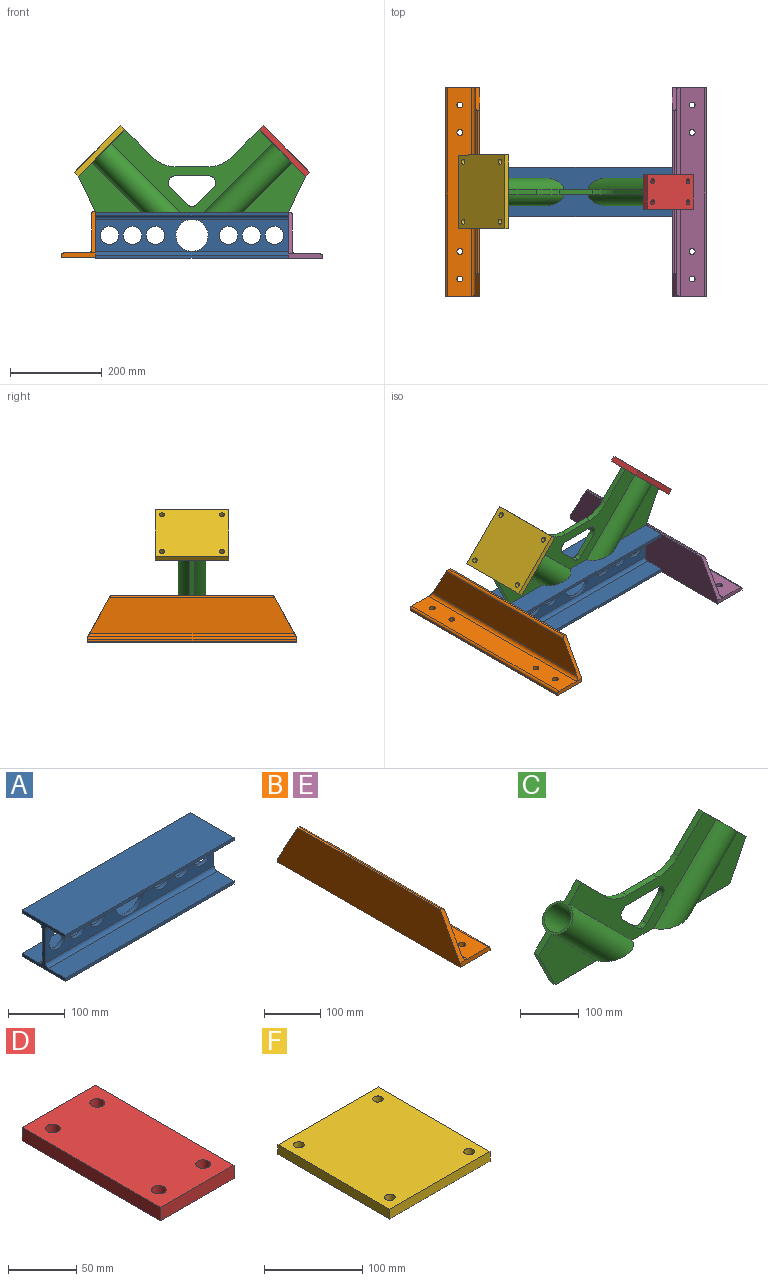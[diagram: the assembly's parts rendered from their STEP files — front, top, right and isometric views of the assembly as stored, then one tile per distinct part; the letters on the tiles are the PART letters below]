
ASSEMBLY  parts=6 mates=5
PART A: 25 faces, bbox 420x108x100 mm
  f0: plane 108x100mm, normal (1,0,0), area 2194.9mm2, adj f9,f10,f11,f12,f13,f14,f15,f16
  f1: cylinder r=35mm len=70mm, axis (0,1,0), area 1759.3mm2, adj f9,f10
  f2: cylinder r=20mm len=40mm, axis (0,1,0), area 1005.3mm2, adj f9,f10
  f3: cylinder r=20mm len=40mm, axis (0,1,0), area 1005.3mm2, adj f9,f10
  f4: cylinder r=20mm len=40mm, axis (0,1,0), area 1005.3mm2, adj f9,f10
  f5: cylinder r=20mm len=40mm, axis (0,1,0), area 1005.3mm2, adj f9,f10
  f6: cylinder r=20mm len=40mm, axis (0,1,0), area 1005.3mm2, adj f9,f10
  f7: cylinder r=20mm len=40mm, axis (0,1,0), area 1005.3mm2, adj f9,f10
  f8: plane 108x100mm, normal (-1,0,0), area 2194.9mm2, adj f9,f10,f11,f12,f13,f14,f15,f16
  f9: plane 420x70.6mm, normal (0,-1,0), area 18263.7mm2, adj f0,f1,f2,f3,f4,f5,f6,f7
  f10: plane 420x70.6mm, normal (0,1,0), area 18263.7mm2, adj f0,f1,f2,f3,f4,f5,f6,f7
  f11: plane 420x42mm, normal (0,0,1), area 17640mm2, adj f0,f8,f14,f24
  f12: plane 420x108mm, normal (0,0,-1), area 45360mm2, adj f0,f8,f14,f15
  f13: plane 420x42mm, normal (0,0,1), area 17640mm2, adj f0,f8,f15,f22
  f14: plane 420x6.7mm, normal (0,-1,0), area 2814mm2, adj f0,f8,f11,f12
  f15: plane 420x6.7mm, normal (0,1,0), area 2814mm2, adj f0,f8,f12,f13
  f16: plane 420x42mm, normal (0,0,-1), area 17640mm2, adj f0,f8,f19,f23
  f17: plane 420x42mm, normal (0,0,-1), area 17640mm2, adj f0,f8,f20,f21
  f18: plane 420x108mm, normal (0,0,1), area 45360mm2, adj f0,f8,f19,f20
  f19: plane 420x6.7mm, normal (0,-1,0), area 2814mm2, adj f0,f8,f16,f18
  f20: plane 420x6.7mm, normal (0,1,0), area 2814mm2, adj f0,f8,f17,f18
  f21: cylinder r=8mm len=420mm, axis (-1,0,0), area 5277.9mm2, adj f0,f8,f10,f17
  f22: cylinder r=8mm len=420mm, axis (1,0,0), area 5277.9mm2, adj f0,f8,f10,f13
  f23: cylinder r=8mm len=420mm, axis (1,0,0), area 5277.9mm2, adj f0,f8,f9,f16
  f24: cylinder r=8mm len=420mm, axis (-1,0,0), area 5277.9mm2, adj f0,f8,f9,f11
PART B: 17 faces, bbox 75x456x100 mm
  f0: plane 356x4.5mm, normal (0,0,1), area 1602mm2, adj f1,f9,f10,f12
  f1: plane 456x100mm, normal (-1,0,0), area 41075mm2, adj f0,f2,f3,f10,f11,f12
  f2: plane 75x9.5mm, normal (0,-1,0), area 707.1mm2, adj f1,f3,f4,f5,f6,f10
  f3: plane 456x75mm, normal (0,0,-1), area 33685.3mm2, adj f1,f2,f4,f11,f13,f14,f15,f16
  f4: plane 456x4.5mm, normal (1,0,0), area 2052mm2, adj f2,f3,f5,f11
  f5: cylinder r=5mm len=456mm, axis (0,-1,0), area 3581.4mm2, adj f2,f4,f6,f11
  f6: plane 456x52.5mm, normal (0,0,1), area 23425.3mm2, adj f2,f5,f7,f11,f13,f14,f15,f16
  f7: cylinder r=8mm len=456mm, axis (0,-1,0), area 5689.9mm2, adj f6,f8,f10,f12
  f8: plane 447.16x77.5mm, normal (1,0,0), area 31336.5mm2, adj f7,f9,f10,f12
  f9: cylinder r=5mm len=361.53mm, axis (0,-1,0), area 2811.8mm2, adj f0,f8,f10,f12
  f10: plane 90.5x50mm, normal (0,-0.88,0.48), area 991.8mm2, adj f0,f1,f2,f7,f8,f9
  f11: plane 75x9.5mm, normal (0,1,0), area 707.1mm2, adj f1,f3,f4,f5,f6,f12
  f12: plane 90.5x50mm, normal (0,0.88,0.48), area 991.8mm2, adj f0,f1,f7,f8,f9,f11
  f13: cylinder r=6.4mm len=12.8mm, axis (0,0,1), area 382mm2, adj f3,f6
  f14: cylinder r=6.4mm len=12.8mm, axis (0,0,1), area 382mm2, adj f3,f6
  f15: cylinder r=6.4mm len=12.8mm, axis (0,0,1), area 382mm2, adj f3,f6
  f16: cylinder r=6.4mm len=12.8mm, axis (0,0,1), area 382mm2, adj f3,f6
PART C: 29 faces, bbox 508.3x71.2x233.8 mm
  f0: plane 139.32x109.32mm, normal (0,-1,0), area 7269.7mm2, adj f11,f12,f13,f26
  f1: plane 139.32x109.32mm, normal (0,1,0), area 7269.7mm2, adj f11,f12,f13,f25
  f2: plane 353.84x181.12mm, normal (0,-1,0), area 18591mm2, adj f4,f5,f6,f7,f8,f9,f10,f11
  f3: plane 353.84x181.12mm, normal (0,1,0), area 18591mm2, adj f4,f5,f6,f7,f8,f9,f10,f11
  f4: cylinder r=15mm len=25.19mm, axis (0,1,0), area 417.2mm2, adj f2,f3,f5,f20
  f5: plane 73.6x12mm, normal (0,0,-1), area 883.2mm2, adj f2,f3,f4,f6
  f6: cylinder r=15mm len=25.19mm, axis (0,1,0), area 417.2mm2, adj f2,f3,f5,f7
  f7: plane 37.21x37.2mm, normal (-0.71,0,0.71), area 631.4mm2, adj f2,f3,f6,f8
  f8: cylinder r=15mm len=12mm, axis (0,1,0), area 141.4mm2, adj f2,f3,f7,f9
  f9: cylinder r=15mm len=12mm, axis (0,1,0), area 141.4mm2, adj f2,f3,f8,f20
  f10: plane 60.61x60.6mm, normal (0.71,0,0.71), area 1028.5mm2, adj f2,f3,f11,f19
  f11: plane 101.83x101.81mm, normal (-0.71,0,0.71), area 1765.7mm2, adj f0,f1,f2,f3,f10,f12,f25,f26
  f12: plane 79.31x38.73mm, normal (-0.9,0,-0.44), area 1059.1mm2, adj f0,f1,f11,f13
  f13: plane 430.87x71.17mm, normal (0,0,-1), area 5146.6mm2, adj f0,f1,f2,f3,f12,f14,f21,f22
  f14: plane 79.31x38.73mm, normal (0.9,0,-0.44), area 1059.1mm2, adj f13,f15,f21,f22
  f15: plane 101.83x101.81mm, normal (0.71,0,0.71), area 1765.7mm2, adj f2,f3,f14,f16,f21,f22,f23,f24
  f16: plane 60.61x60.6mm, normal (-0.71,0,0.71), area 1028.5mm2, adj f2,f3,f15,f17
  f17: cylinder r=70mm len=49.5mm, axis (0,1,0), area 659.8mm2, adj f2,f3,f16,f18
  f18: plane 73.6x12mm, normal (0,0,1), area 883.2mm2, adj f2,f3,f17,f19
  f19: cylinder r=70mm len=49.5mm, axis (0,1,0), area 659.8mm2, adj f2,f3,f10,f18
  f20: plane 37.21x37.2mm, normal (0.71,0,0.71), area 631.4mm2, adj f2,f3,f4,f9
  f21: plane 139.32x109.32mm, normal (0,-1,0), area 7269.7mm2, adj f13,f14,f15,f24
  f22: plane 139.32x109.32mm, normal (0,1,0), area 7269.7mm2, adj f13,f14,f15,f23
  f23: cylinder r=30.15mm len=192.88mm, axis (0.71,0,0.71), area 15215.8mm2, adj f3,f13,f15,f22
  f24: cylinder r=30.15mm len=192.88mm, axis (0.71,0,0.71), area 15215.8mm2, adj f2,f13,f15,f21
  f25: cylinder r=30.15mm len=192.88mm, axis (-0.71,0,0.71), area 15215.8mm2, adj f1,f3,f11,f13
  f26: cylinder r=30.15mm len=192.88mm, axis (-0.71,0,0.71), area 15215.8mm2, adj f0,f2,f11,f13
  f27: cylinder r=25.85mm len=185.29mm, axis (0.71,0,0.71), area 29905.7mm2, adj f13,f15
  f28: cylinder r=25.85mm len=185.04mm, axis (-0.71,0,0.71), area 29905.7mm2, adj f11,f13
PART D: 10 faces, bbox 76x144x12 mm
  f0: plane 76x12mm, normal (0,-1,0), area 912mm2, adj f1,f3,f4,f5
  f1: plane 144x12mm, normal (1,0,0), area 1728mm2, adj f0,f2,f4,f5
  f2: plane 76x12mm, normal (0,1,0), area 912mm2, adj f1,f3,f4,f5
  f3: plane 144x12mm, normal (-1,0,0), area 1728mm2, adj f0,f2,f4,f5
  f4: plane 144x76mm, normal (0,0,-1), area 10577.6mm2, adj f0,f1,f2,f3,f6,f7,f8,f9
  f5: plane 144x76mm, normal (0,0,1), area 10577.6mm2, adj f0,f1,f2,f3,f6,f7,f8,f9
  f6: cylinder r=5.4mm len=12mm, axis (0,0,1), area 407.2mm2, adj f4,f5
  f7: cylinder r=5.4mm len=12mm, axis (0,0,1), area 407.2mm2, adj f4,f5
  f8: cylinder r=5.4mm len=12mm, axis (0,0,1), area 407.2mm2, adj f4,f5
  f9: cylinder r=5.4mm len=12mm, axis (0,0,1), area 407.2mm2, adj f4,f5
PART E: same geometry as B
PART F: 10 faces, bbox 144x161x12 mm
  f0: plane 161x12mm, normal (1,0,0), area 1932mm2, adj f1,f3,f4,f5
  f1: plane 144x12mm, normal (0,1,0), area 1728mm2, adj f0,f2,f4,f5
  f2: plane 161x12mm, normal (-1,0,0), area 1932mm2, adj f1,f3,f4,f5
  f3: plane 144x12mm, normal (0,-1,0), area 1728mm2, adj f0,f2,f4,f5
  f4: plane 161x144mm, normal (0,0,-1), area 22817.6mm2, adj f0,f1,f2,f3,f6,f7,f8,f9
  f5: plane 161x144mm, normal (0,0,1), area 22817.6mm2, adj f0,f1,f2,f3,f6,f7,f8,f9
  f6: cylinder r=5.4mm len=12mm, axis (0,0,1), area 407.2mm2, adj f4,f5
  f7: cylinder r=5.4mm len=12mm, axis (0,0,1), area 407.2mm2, adj f4,f5
  f8: cylinder r=5.4mm len=12mm, axis (0,0,1), area 407.2mm2, adj f4,f5
  f9: cylinder r=5.4mm len=12mm, axis (0,0,1), area 407.2mm2, adj f4,f5
PLACE A rot(axis=(0,0,1),0deg) t=(-165.02,42.06,-32.82)mm
PLACE B rot(axis=(0,0,1),180deg) t=(-375.02,270.06,-80.63)mm
PLACE C rot(axis=(-0.5,0,0.87),0deg) t=(-165.02,48.06,17.18)mm
PLACE D rot(axis=(0.36,0.36,0.86),98.4deg) t=(41.28,42.06,155.88)mm
PLACE E t=(44.98,-185.94,-82.82)mm
PLACE F rot(axis=(0,-1,0),45deg) t=(-371.32,42.06,155.88)mm
MATE fastened C.f13 <-> A.f18  axis (0,0,-1) through (-165.02,42.06,17.18)mm
MATE fastened A.f8 <-> B.f1  axis (-1,0,0) through (-375.02,42.06,-32.82)mm
MATE fastened A.f0 <-> E.f1  axis (1,0,0) through (44.98,42.06,17.18)mm
MATE fastened D.f4 <-> C.f27  axis (-0.71,0,-0.71) through (32.79,42.06,147.39)mm
MATE fastened F.f4 <-> C.f28  axis (0.71,0,-0.71) through (-362.84,42.06,147.39)mm
